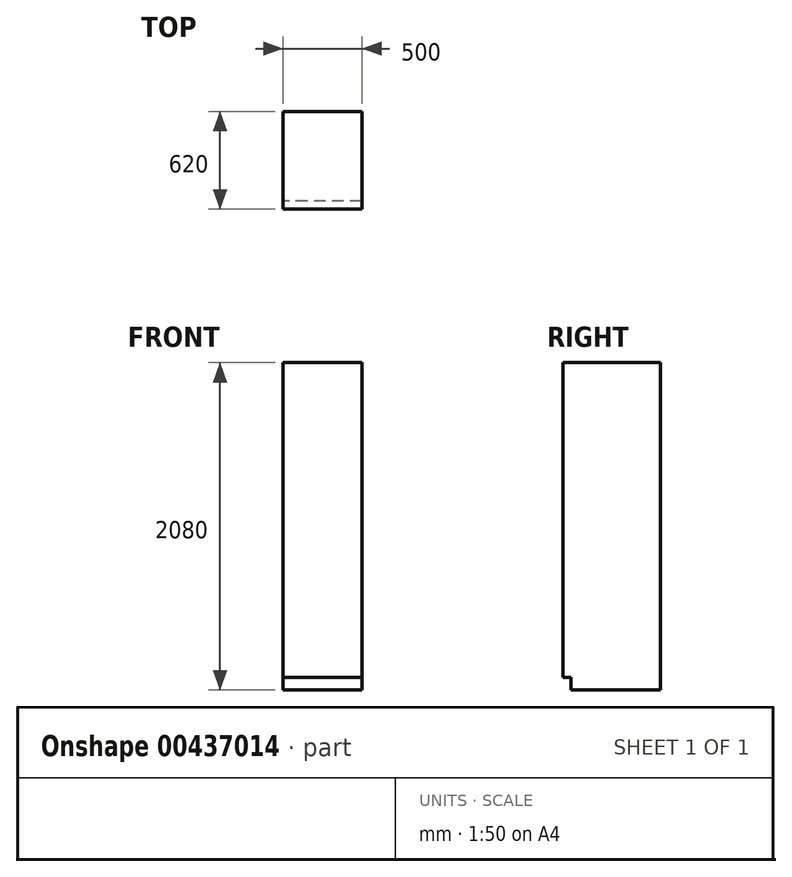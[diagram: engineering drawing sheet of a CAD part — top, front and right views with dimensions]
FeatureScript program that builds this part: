
annotation { "Feature Type Name" : "Feature", "Feature Type Description" : "" }
export const myFeature = defineFeature(function(context is Context, id is Id, definition is map)
    precondition{}
    {
        {
            var Q0;
            Q0=qCreatedBy(makeId("Right.planeOp"),FACE);
            var sketch = newSketch(context, id + "F0", { "sketchPlane" : qUnion([Q0])});
            skLineSegment(sketch, "E0.bottom", {"start": v(0, 0) * mm, "end": v(-570, 0) * mm});
            skLineSegment(sketch, "E0.top", {"start": v(0, 2080) * mm, "end": v(-620, 2080) * mm});
            skLineSegment(sketch, "E0.left", {"start": v(0, 0) * mm, "end": v(0, 2080) * mm});
            skLineSegment(sketch, "E0.right", {"start": v(-620, 80) * mm, "end": v(-620, 2080) * mm});
            skLineSegment(sketch, "E1.top", {"start": v(-620, 80) * mm, "end": v(-570, 80) * mm});
            skLineSegment(sketch, "E1.right", {"start": v(-570, 0) * mm, "end": v(-570, 80) * mm});
            skSolve(sketch);
        }
        {
            var Q0;
            Q0=qSketchRegion(id+"F0",true);
            extrude(context, id + "F1", {"entities" : qUnion([Q0]), "depth" : 500 * mm});
        }
    });
